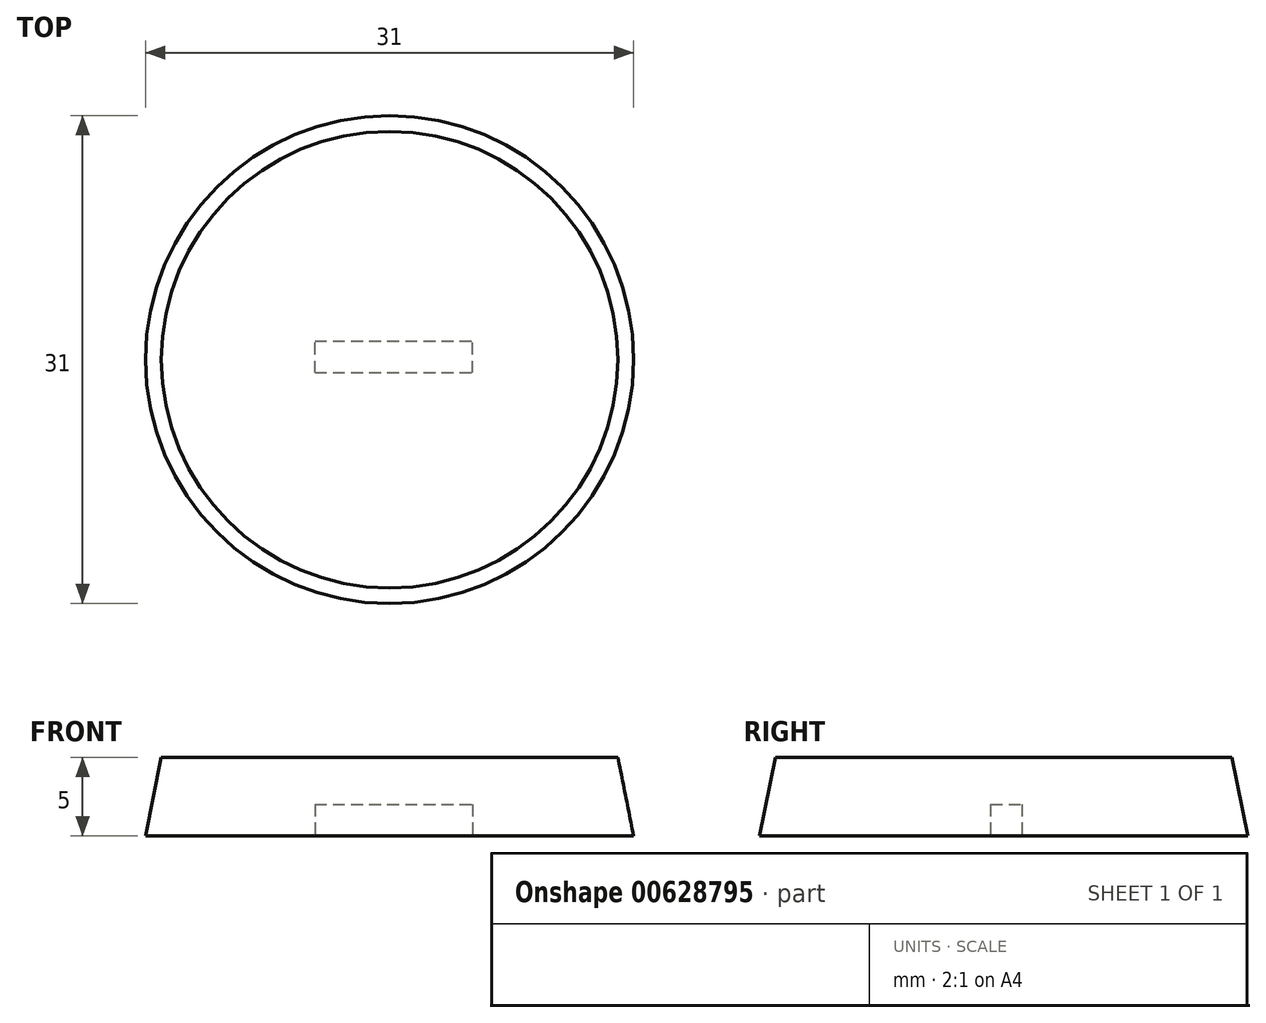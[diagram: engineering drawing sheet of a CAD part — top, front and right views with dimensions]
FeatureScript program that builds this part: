
annotation { "Feature Type Name" : "Feature", "Feature Type Description" : "" }
export const myFeature = defineFeature(function(context is Context, id is Id, definition is map)
    precondition{}
    {
        {
            var Q0;
            Q0=qCreatedBy(makeId("Top.planeOp"),FACE);
            var sketch = newSketch(context, id + "F0", { "sketchPlane" : qUnion([Q0])});
            skCircle(sketch, "E0", {"center": v(0, 0) * mm, "radius": 15.5 * mm});
            skSolve(sketch);
        }
        {
            var Q0;
            Q0 = qSketchRegion(id + "F0", true);
            extrude(context, id + "F1", {"entities" : qUnion([Q0]), "depth" : 5 * mm, "offsetDistance" : 25 * mm});
        }
        {
            var Q0;
            Q0=makeQuery(id+"F1.opExtrude","CAP_EDGE",EDGE,{"disambiguationData":[OSD([sQuery(id+"F0.wireOp",EDGE,"E0")])],"isStart":false});
            chamfer(context, id + "F2", {"entities" : qUnion([Q0]), "chamferType" : ChamferType.TWO_OFFSETS, "width1" : 1 * mm, "oppositeDirection" : false, "width2" : 5 * mm, "tangentPropagation" : true});
        }
        {
            var Q0;
            Q0=makeQuery(id+"F1.opExtrude","CAP_FACE",FACE,{"disambiguationData":[OSD([sQuery(id+"F0.wireOp",EDGE,"E0")])],"isStart":true});
            var sketch = newSketch(context, id + "F3", { "sketchPlane" : qUnion([Q0])});
            skLineSegment(sketch, "E1.bottom", {"start": v(-4.74, 0.82) * mm, "end": v(5.26, 0.82) * mm});
            skLineSegment(sketch, "E1.top", {"start": v(-4.74, -1.18) * mm, "end": v(5.26, -1.18) * mm});
            skLineSegment(sketch, "E1.left", {"start": v(-4.74, 0.82) * mm, "end": v(-4.74, -1.18) * mm});
            skLineSegment(sketch, "E1.right", {"start": v(5.26, 0.82) * mm, "end": v(5.26, -1.18) * mm});
            skSolve(sketch);
        }
        {
            var Q0;
            Q0 = qSketchRegion(id + "F3", true);
            extrude(context, id + "F4", {"entities" : qUnion([Q0]), "operationType" : NewBodyOperationType.REMOVE, "oppositeDirection" : true, "depth" : 2 * mm, "offsetDistance" : 25 * mm});
        }
    });
